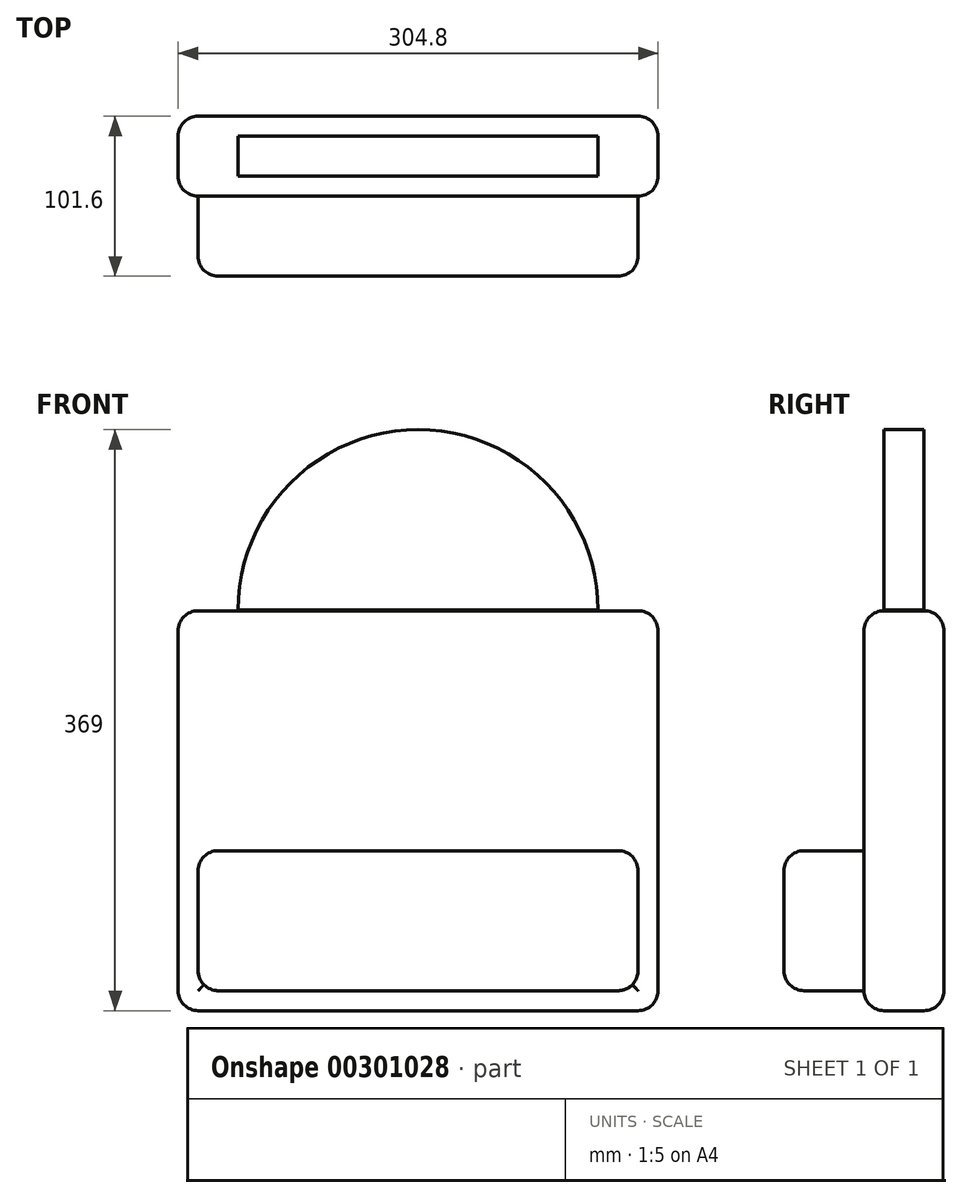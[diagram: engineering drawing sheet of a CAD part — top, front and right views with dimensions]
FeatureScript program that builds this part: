
annotation { "Feature Type Name" : "Feature", "Feature Type Description" : "" }
export const myFeature = defineFeature(function(context is Context, id is Id, definition is map)
    precondition{}
    {
        {
            var Q0;
            Q0=qCreatedBy(makeId("Front.planeOp"),FACE);
            var sketch = newSketch(context, id + "F0", { "sketchPlane" : qUnion([Q0])});
            skLineSegment(sketch, "E0.bottom", {"start": v(152.4, -127) * mm, "end": v(-152.4, -127) * mm});
            skLineSegment(sketch, "E0.top", {"start": v(152.4, 127) * mm, "end": v(-152.4, 127) * mm});
            skLineSegment(sketch, "E0.left", {"start": v(152.4, -127) * mm, "end": v(152.4, 127) * mm});
            skLineSegment(sketch, "E0.right", {"start": v(-152.4, -127) * mm, "end": v(-152.4, 127) * mm});
            skPoint(sketch, "E0.middle", {"position": v(0, 0) * mm});
            skSolve(sketch);
        }
        {
            var Q0;
            Q0 = qSketchRegion(id + "F0", true);
            extrude(context, id + "F1", {"entities" : qUnion([Q0]), "depth" : 25.4 * mm, "hasSecondDirection" : true, "secondDirectionOppositeDirection" : true, "secondDirectionDepth" : 25.4 * mm});
        }
        {
            var Q0;
            Q0=makeQuery(id+"F1.opExtrude","CAP_FACE",FACE,{"disambiguationData":[OSD([sQuery(id+"F0.wireOp",EDGE,"E0.bottom"),sQuery(id+"F0.wireOp",EDGE,"E0.top"),sQuery(id+"F0.wireOp",EDGE,"E0.left"),sQuery(id+"F0.wireOp",EDGE,"E0.right")])],"isStart":false});
            var Q1;
            Q1=makeQuery(id+"F1.opExtrude","CAP_FACE",FACE,{"disambiguationData":[OSD([sQuery(id+"F0.wireOp",EDGE,"E0.bottom"),sQuery(id+"F0.wireOp",EDGE,"E0.top"),sQuery(id+"F0.wireOp",EDGE,"E0.left"),sQuery(id+"F0.wireOp",EDGE,"E0.right")])],"isStart":true});
            var Q2;
            Q2=makeQuery(id+"F1.opExtrude","SWEPT_FACE",FACE,{"disambiguationData":[OSD([sQuery(id+"F0.wireOp",EDGE,"E0.left")])]});
            var Q3;
            Q3=makeQuery(id+"F1.opExtrude","SWEPT_FACE",FACE,{"disambiguationData":[OSD([sQuery(id+"F0.wireOp",EDGE,"E0.top")])]});
            var Q4;
            Q4=makeQuery(id+"F1.opExtrude","SWEPT_FACE",FACE,{"disambiguationData":[OSD([sQuery(id+"F0.wireOp",EDGE,"E0.bottom")])]});
            fillet(context, id + "F2", {"entities" : qUnion([Q0, Q1, Q2, Q3, Q4]), "radius" : 12.7 * mm, "tangentPropagation" : true, "allowEdgeOverflow" : false});
        }
        {
            var Q0;
            Q0=makeQuery(id+"F1.opExtrude","CAP_FACE",FACE,{"disambiguationData":[OSD([sQuery(id+"F0.wireOp",EDGE,"E0.bottom"),sQuery(id+"F0.wireOp",EDGE,"E0.top"),sQuery(id+"F0.wireOp",EDGE,"E0.left"),sQuery(id+"F0.wireOp",EDGE,"E0.right")])],"isStart":false});
            var sketch = newSketch(context, id + "F3", { "sketchPlane" : qUnion([Q0])});
            skLineSegment(sketch, "E1.bottom", {"start": v(-139.7, -114.3) * mm, "end": v(139.7, -114.3) * mm});
            skLineSegment(sketch, "E1.top", {"start": v(-139.7, -25.4) * mm, "end": v(139.7, -25.4) * mm});
            skLineSegment(sketch, "E1.left", {"start": v(-139.7, -114.3) * mm, "end": v(-139.7, -25.4) * mm});
            skLineSegment(sketch, "E1.right", {"start": v(139.7, -114.3) * mm, "end": v(139.7, -25.4) * mm});
            skSolve(sketch);
        }
        {
            var Q0;
            Q0 = qSketchRegion(id + "F3", true);
            extrude(context, id + "F4", {"entities" : qUnion([Q0]), "operationType" : NewBodyOperationType.ADD, "depth" : 50.8 * mm});
        }
        {
            var Q0;
            Q0=makeQuery(id+"F4.opExtrude","CAP_EDGE",EDGE,{"disambiguationData":[OSD([sQuery(id+"F3.wireOp",EDGE,"E1.top")])],"isStart":false});
            var Q1;
            Q1=makeQuery(id+"F4.opExtrude","CAP_EDGE",EDGE,{"disambiguationData":[OSD([sQuery(id+"F3.wireOp",EDGE,"E1.right")])],"isStart":false});
            var Q2;
            Q2=makeQuery(id+"F4.opExtrude","CAP_EDGE",EDGE,{"disambiguationData":[OSD([sQuery(id+"F3.wireOp",EDGE,"E1.bottom")])],"isStart":false});
            var Q3;
            Q3=makeQuery(id+"F4.opExtrude","CAP_EDGE",EDGE,{"disambiguationData":[OSD([sQuery(id+"F3.wireOp",EDGE,"E1.left")])],"isStart":false});
            var Q4;
            Q4=makeQuery(id+"F4.opExtrude","SWEPT_EDGE",EDGE,{"disambiguationData":[OSD([sQuery(id+"F3.wireOp",EDGE,"E1.bottom"),sQuery(id+"F3.wireOp",EDGE,"E1.left")])]});
            var Q5;
            Q5=makeQuery(id+"F4.opExtrude","SWEPT_EDGE",EDGE,{"disambiguationData":[OSD([sQuery(id+"F0.wireOp",EDGE,"E0.bottom"),sQuery(id+"F0.wireOp",EDGE,"E0.top"),sQuery(id+"F0.wireOp",EDGE,"E0.left"),sQuery(id+"F0.wireOp",EDGE,"E0.right"),sQuery(id+"F3.wireOp",EDGE,"E1.top"),sQuery(id+"F3.wireOp",EDGE,"E1.left")])]});
            var Q6;
            Q6=makeQuery(id+"F4.opExtrude","SWEPT_EDGE",EDGE,{"disambiguationData":[OSD([sQuery(id+"F3.wireOp",EDGE,"E1.bottom"),sQuery(id+"F3.wireOp",EDGE,"E1.right")])]});
            var Q7;
            Q7=makeQuery(id+"F4.opExtrude","SWEPT_EDGE",EDGE,{"disambiguationData":[OSD([sQuery(id+"F0.wireOp",EDGE,"E0.bottom"),sQuery(id+"F0.wireOp",EDGE,"E0.top"),sQuery(id+"F0.wireOp",EDGE,"E0.left"),sQuery(id+"F0.wireOp",EDGE,"E0.right"),sQuery(id+"F3.wireOp",EDGE,"E1.top"),sQuery(id+"F3.wireOp",EDGE,"E1.right")])]});
            fillet(context, id + "F5", {"entities" : qUnion([Q0, Q1, Q2, Q3, Q4, Q5, Q6, Q7]), "radius" : 12.7 * mm, "tangentPropagation" : true, "allowEdgeOverflow" : false});
        }
        {
            var Q0;
            Q0=qCreatedBy(makeId("Front.planeOp"),FACE);
            var sketch = newSketch(context, id + "F6", { "sketchPlane" : qUnion([Q0])});
            skArc(sketch, "E2", {"start": v(114.3, 127.38) * mm, "mid": v(0, 242) * mm, "end": v(-114.3, 127.38) * mm});
            skLineSegment(sketch, "E3", {"start": v(-114.3, 127.38) * mm, "end": v(114.3, 127.38) * mm});
            skSolve(sketch);
        }
        {
            var Q0;
            Q0 = qSketchRegion(id + "F6", true);
            extrude(context, id + "F7", {"entities" : qUnion([Q0]), "depth" : 12.7 * mm, "hasSecondDirection" : true, "secondDirectionOppositeDirection" : true, "secondDirectionDepth" : 12.7 * mm});
        }
    });
